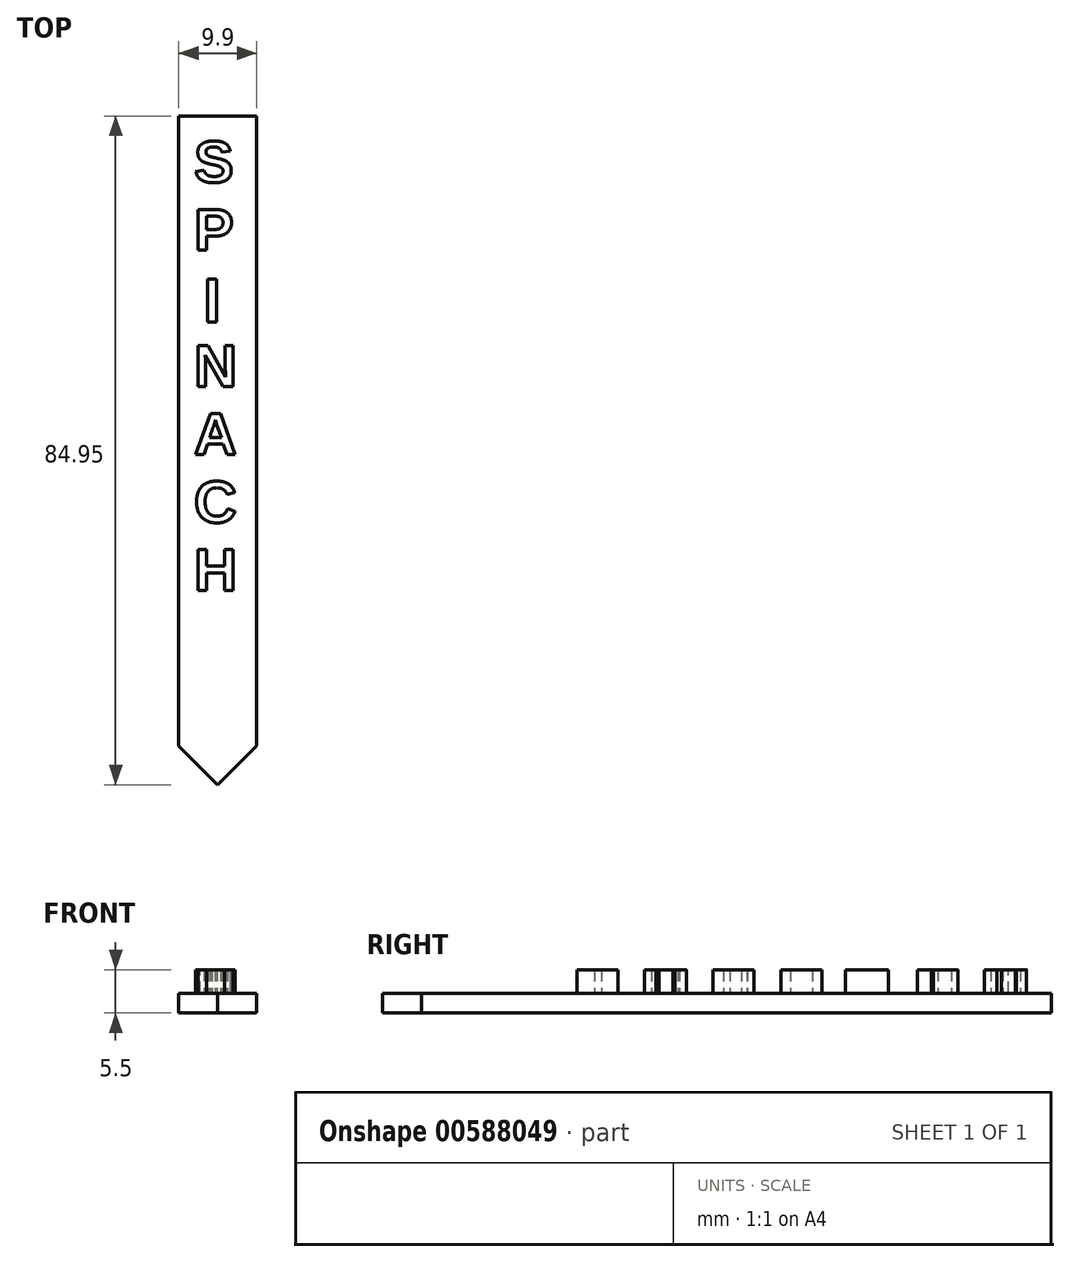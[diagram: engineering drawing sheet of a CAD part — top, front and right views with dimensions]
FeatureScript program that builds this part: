
annotation { "Feature Type Name" : "Feature", "Feature Type Description" : "" }
export const myFeature = defineFeature(function(context is Context, id is Id, definition is map)
    precondition{}
    {
        {
            var Q0;
            Q0=qCreatedBy(makeId("Top.planeOp"),FACE);
            var sketch = newSketch(context, id + "F0", { "sketchPlane" : qUnion([Q0])});
            skLineSegment(sketch, "E0", {"start": v(0, 0) * mm, "end": v(4.95, 4.95) * mm});
            skLineSegment(sketch, "E1", {"start": v(0, 0) * mm, "end": v(-4.95, 4.95) * mm});
            skPoint(sketch, "E2.end.orphan", {"position": v(-3.53, 0) * mm});
            skPoint(sketch, "E3.end.orphan", {"position": v(4.95, 0) * mm});
            skLineSegment(sketch, "E4", {"start": v(4.95, 4.95) * mm, "end": v(4.95, 84.95) * mm});
            skLineSegment(sketch, "E5", {"start": v(-4.95, 4.95) * mm, "end": v(-4.95, 84.95) * mm});
            skLineSegment(sketch, "E6", {"start": v(-4.95, 84.95) * mm, "end": v(4.95, 84.95) * mm});
            skSolve(sketch);
        }
        {
            var Q0;
            Q0=qSketchRegion(id+"F0",true);
            extrude(context, id + "F1", {"entities" : qUnion([Q0]), "depth" : 2.5 * mm, "offsetDistance" : 25 * mm});
        }
        {
            var Q0;
            Q0=makeQuery(id+"F1.opExtrude","CAP_FACE",FACE,{"disambiguationData":[OSD([sQuery(id+"F0.wireOp",EDGE,"E0"),sQuery(id+"F0.wireOp",EDGE,"E1"),sQuery(id+"F0.wireOp",EDGE,"E4"),sQuery(id+"F0.wireOp",EDGE,"E5"),sQuery(id+"F0.wireOp",EDGE,"E6")])],"isStart":false});
            var sketch = newSketch(context, id + "F2", { "sketchPlane" : qUnion([Q0])});
            skText(sketch, "E7", { "text": "S\nP\n\nN\nA\nC\nH", "fontName": "Arimo-Bold.ttf"});
            skText(sketch, "E8", { "text": "I", "fontName": "Arimo-Bold.ttf"});
            const initialGuessF2  = {"E7": [-0.003, 0.07654, 1, 0, 0.00541], "E8": [-0.0018, 0.05877, 1, 0, 0.00575]};
            skSetInitialGuess(sketch, initialGuessF2);
            skSolve(sketch);
        }
        {
            var Q0;
            Q0=qSketchRegion(id+"F2",true);
            extrude(context, id + "F3", {"entities" : qUnion([Q0]), "operationType" : NewBodyOperationType.ADD, "depth" : 3 * mm, "offsetDistance" : 25 * mm});
        }
    });
